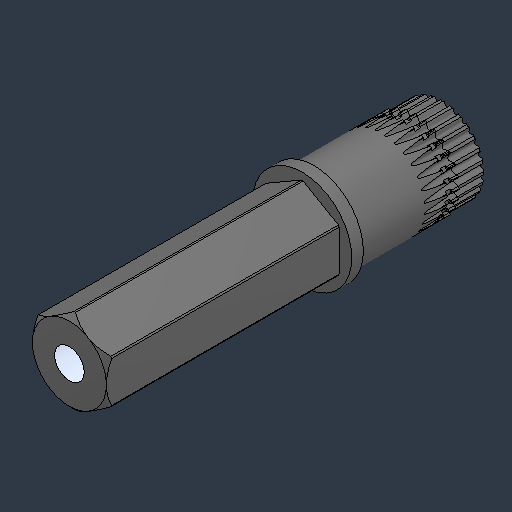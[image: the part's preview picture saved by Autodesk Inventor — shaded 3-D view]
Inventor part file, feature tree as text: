
AUTODESK INVENTOR PART (.ipt)
format: ipt  version: 2024.3 (Build 283343000, 343)  size: 1,331,712 bytes
history: native  units: in
note: dims shown in document units (in); Inventor stores cm internally (conversion verified against a paired STEP export)
features: fillet x1
ambient origin geometry x8: Origin, YZ Plane, XZ Plane, XY Plane, X Axis, Y Axis, Z Axis, Center Point
bodies: Solid1 (feature_tree)
feature tree (1):
  fillet  "Fillet5"  [1 undecoded]
note: 1 required parameter value undecoded (feature->parameter linkage not recoverable at this tier; creation-order binding heuristic only, values carry confidence <= 0.55)
